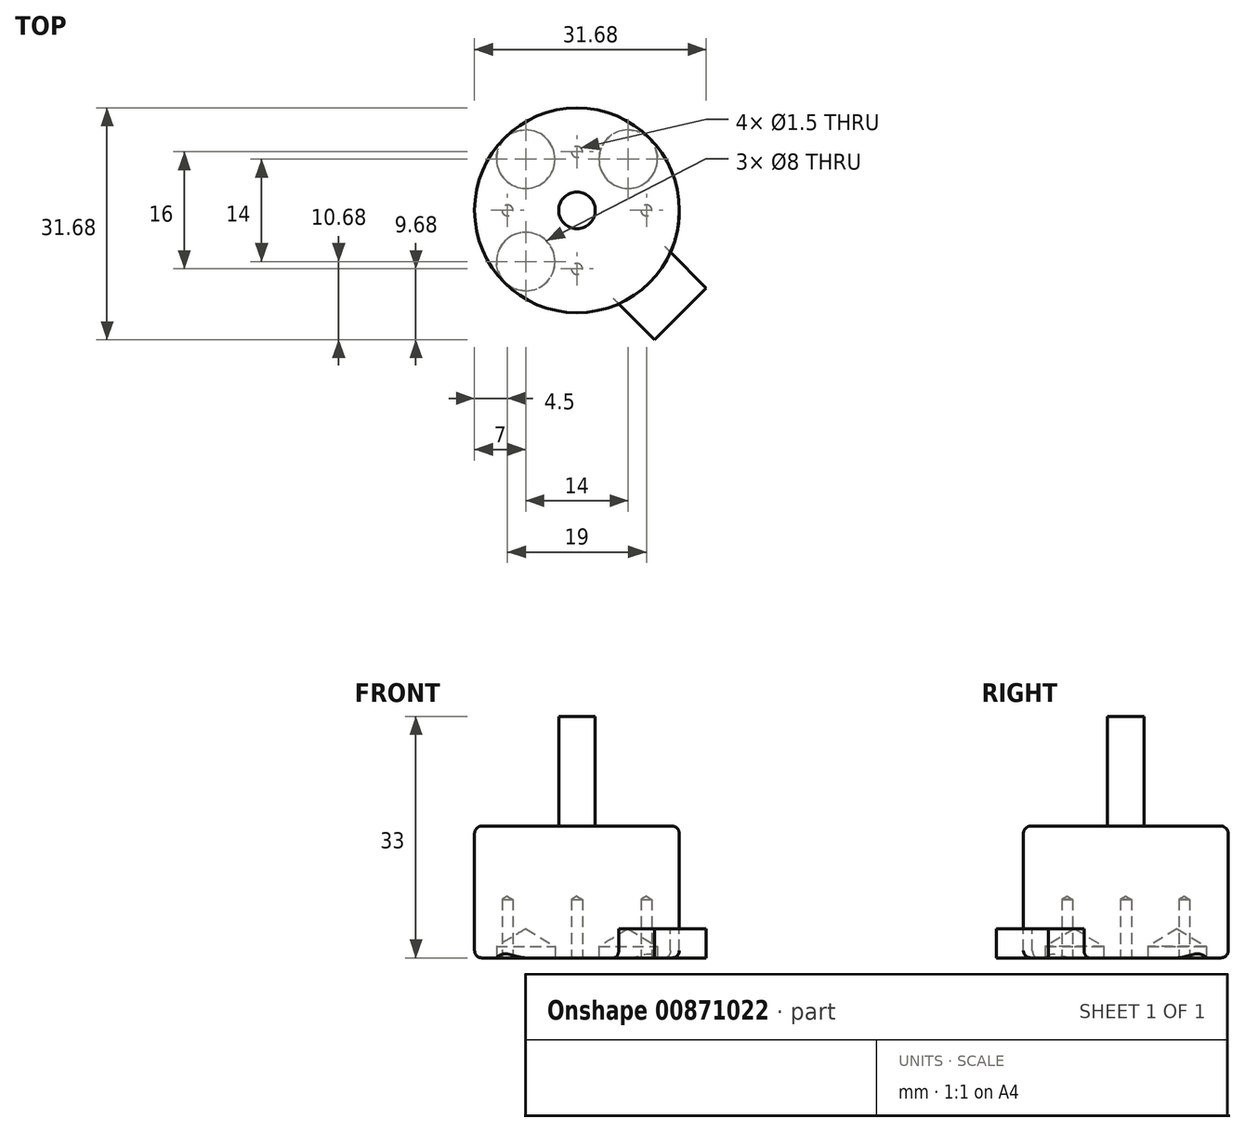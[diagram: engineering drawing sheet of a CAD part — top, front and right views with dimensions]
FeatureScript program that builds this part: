
annotation { "Feature Type Name" : "Feature", "Feature Type Description" : "" }
export const myFeature = defineFeature(function(context is Context, id is Id, definition is map)
    precondition{}
    {
        {
            var Q0;
            Q0=qCreatedBy(makeId("Front.planeOp"),FACE);
            var sketch = newSketch(context, id + "F0", { "sketchPlane" : qUnion([Q0])});
            skLineSegment(sketch, "E0", {"start": v(0, 0) * mm, "end": v(13, 0) * mm});
            skLineSegment(sketch, "E1", {"start": v(14, 1) * mm, "end": v(14, 17) * mm});
            skLineSegment(sketch, "E2", {"start": v(13, 18) * mm, "end": v(2.5, 18) * mm});
            skLineSegment(sketch, "E3", {"start": v(2.5, 18) * mm, "end": v(2.5, 33) * mm});
            skLineSegment(sketch, "E4", {"start": v(2.5, 33) * mm, "end": v(0, 33) * mm});
            skLineSegment(sketch, "E5", {"start": v(0, 33) * mm, "end": v(0, 0) * mm});
            skPoint(sketch, "E6.visualSharp", {"position": v(14, 18) * mm});
            skArc(sketch, "E6.filletArc", {"start": v(14, 17) * mm, "mid": v(13.7, 17.7) * mm, "end": v(13, 18) * mm});
            skPoint(sketch, "E7.visualSharp", {"position": v(14, 0) * mm});
            skArc(sketch, "E7.filletArc", {"start": v(13, 0) * mm, "mid": v(13.7, 0.3) * mm, "end": v(14, 1) * mm});
            skSolve(sketch);
        }
        {
            var Q0;
            Q0=makeQuery(id+"F0.imprint","IMPRINT",FACE,{"disambiguationData":[TD([[makeQuery(id+"F0.imprint","IMPRINT",EDGE,{"derivedFrom":sQuery(id+"F0.wireOp",EDGE,"E0")}),1.0]])]});
            var Q1;
            Q1=sQuery(id+"F0.wireOp",EDGE,"E5");
            revolve(context, id + "F1", {"surfaceOperationType" : NewSurfaceOperationType.NEW, "entities" : qUnion([Q0]), "axis" : qUnion([Q1]), "revolveType" : RevolveType.FULL});
        }
        {
            var Q0;
            Q0=makeQuery(id+"F1.opRevolve","SWEPT_FACE",FACE,{"disambiguationData":[OSD([sQuery(id+"F0.wireOp",EDGE,"E0")])]});
            var sketch = newSketch(context, id + "F2", { "sketchPlane" : qUnion([Q0])});
            skPoint(sketch, "E8", {"position": v(0, 8) * mm});
            skPoint(sketch, "E9", {"position": v(0, -8) * mm});
            skPoint(sketch, "E10", {"position": v(-9.5, 0) * mm});
            skPoint(sketch, "E11", {"position": v(9.5, 0) * mm});
            skSolve(sketch);
        }
        {
            var Q0;
            Q0=sQuery(id+"F2.wireOp",VERTEX,"E8");
            var Q1;
            Q1=sQuery(id+"F2.wireOp",VERTEX,"E10");
            var Q2;
            Q2=sQuery(id+"F2.wireOp",VERTEX,"E9");
            var Q3;
            Q3=sQuery(id+"F2.wireOp",VERTEX,"E11");
            var Q4;
            Q4=makeQuery(id+"F1.opRevolve","SWEPT_BODY",BODY,{"disambiguationData":[OSD([sQuery(id+"F0.wireOp",EDGE,"E0"),sQuery(id+"F0.wireOp",EDGE,"E1"),sQuery(id+"F0.wireOp",EDGE,"E2"),sQuery(id+"F0.wireOp",EDGE,"E3"),sQuery(id+"F0.wireOp",EDGE,"E4"),sQuery(id+"F0.wireOp",EDGE,"E5"),sQuery(id+"F0.wireOp",EDGE,"E6.filletArc"),sQuery(id+"F0.wireOp",EDGE,"E7.filletArc")])]});
            hole(context, id + "F3", {"style" : HoleStyle.SIMPLE, "endStyle" : HoleEndStyle.BLIND, "holeDiameter" : 1.5 * mm, "majorDiameter" : 5 * mm, "holeDepth" : 8 * mm, "isTappedThrough" : true, "tappedDepth" : 12 * mm, "tapClearance" : 3, "locations" : qUnion([Q0, Q1, Q2, Q3]), "scope" : qUnion([Q4])});
        }
        {
            var Q0;
            Q0=makeQuery(id+"F1.opRevolve","SWEPT_FACE",FACE,{"disambiguationData":[OSD([sQuery(id+"F0.wireOp",EDGE,"E0")])]});
            var sketch = newSketch(context, id + "F4", { "sketchPlane" : qUnion([Q0])});
            skLineSegment(sketch, "E12", {"start": v(20.5, 0) * mm, "end": v(0, 0) * mm});
            skLineSegment(sketch, "E13", {"start": v(0, 0) * mm, "end": v(16.66, 16.66) * mm});
            skPoint(sketch, "E14", {"position": v(16.66, 16.66) * mm});
            skSolve(sketch);
        }
        {
            var Q0;
            Q0=makeQuery(id+"F1.opRevolve","SWEPT_FACE",FACE,{"disambiguationData":[OSD([sQuery(id+"F0.wireOp",EDGE,"E4")])]});
            var sketch = newSketch(context, id + "F5", { "sketchPlane" : qUnion([Q0])});
            skPoint(sketch, "E15", {"position": v(0, 0) * mm});
            skSolve(sketch);
        }
        {
            var Q0;
            Q0=sQuery(id+"F5.wireOp",VERTEX,"E15");
            var Q1;
            Q1=sQuery(id+"F4.wireOp",VERTEX,"E12.end");
            var Q2;
            Q2=sQuery(id+"F4.wireOp",VERTEX,"E14");
            cPlane(context, id + "F6", {"entities" : qUnion([Q0, Q1, Q2]), "cplaneType" : CPlaneType.THREE_POINT, "offset" : 25 * mm, "width" : 150 * mm, "height" : 150 * mm});
        }
        {
            var Q0;
            Q0=qCreatedBy(id+"F6.planeOp",FACE);
            var sketch = newSketch(context, id + "F7", { "sketchPlane" : qUnion([Q0])});
            skLineSegment(sketch, "E16.bottom", {"start": v(-11, 0) * mm, "end": v(-20, 0) * mm});
            skLineSegment(sketch, "E16.top", {"start": v(-11, 4) * mm, "end": v(-20, 4) * mm});
            skLineSegment(sketch, "E16.left", {"start": v(-11, 0) * mm, "end": v(-11, 4) * mm});
            skLineSegment(sketch, "E16.right", {"start": v(-20, 0) * mm, "end": v(-20, 4) * mm});
            skSolve(sketch);
        }
        {
            var Q0;
            Q0=makeQuery(id+"F7.imprint","IMPRINT",FACE,{"disambiguationData":[TD([[makeQuery(id+"F7.imprint","IMPRINT",EDGE,{"derivedFrom":sQuery(id+"F7.wireOp",EDGE,"E16.bottom")}),-1.0]])]});
            extrude(context, id + "F8", {"entities" : qUnion([Q0]), "operationType" : NewBodyOperationType.ADD, "endBound" : BoundingType.SYMMETRIC, "depth" : 10 * mm, "offsetDistance" : 25 * mm});
        }
        {
            var Q0;
            Q0=makeQuery(id+"F8.boolean.opBoolean","MERGE",FACE,{"derivedFrom":[makeQuery(id+"F1.opRevolve","SWEPT_FACE",FACE,{"disambiguationData":[OSD([sQuery(id+"F0.wireOp",EDGE,"E0")])]}),makeQuery(id+"F8.opExtrude","SWEPT_FACE",FACE,{"disambiguationData":[OSD([sQuery(id+"F7.wireOp",EDGE,"E16.bottom")])]})]});
            var sketch = newSketch(context, id + "F9", { "sketchPlane" : qUnion([Q0])});
            skLineSegment(sketch, "E17", {"start": v(0, 0) * mm, "end": v(-13.01, 13.01) * mm});
            skLineSegment(sketch, "E18", {"start": v(0, 0) * mm, "end": v(-13.82, -13.82) * mm});
            skLineSegment(sketch, "E19", {"start": v(0, 0) * mm, "end": v(14.67, -14.67) * mm});
            skPoint(sketch, "E20", {"position": v(-7, 7) * mm});
            skPoint(sketch, "E21", {"position": v(-7, -7) * mm});
            skPoint(sketch, "E22", {"position": v(7, -7) * mm});
            skSolve(sketch);
        }
        {
            var Q0;
            Q0=sQuery(id+"F9.wireOp",VERTEX,"E20");
            var Q1;
            Q1=sQuery(id+"F9.wireOp",VERTEX,"E21");
            var Q2;
            Q2=sQuery(id+"F9.wireOp",VERTEX,"E22");
            var Q3;
            Q3=makeQuery(id+"F1.opRevolve","SWEPT_BODY",BODY,{"disambiguationData":[OSD([sQuery(id+"F0.wireOp",EDGE,"E0"),sQuery(id+"F0.wireOp",EDGE,"E1"),sQuery(id+"F0.wireOp",EDGE,"E2"),sQuery(id+"F0.wireOp",EDGE,"E3"),sQuery(id+"F0.wireOp",EDGE,"E4"),sQuery(id+"F0.wireOp",EDGE,"E5"),sQuery(id+"F0.wireOp",EDGE,"E6.filletArc"),sQuery(id+"F0.wireOp",EDGE,"E7.filletArc")])]});
            hole(context, id + "F10", {"style" : HoleStyle.SIMPLE, "endStyle" : HoleEndStyle.BLIND, "holeDiameter" : 8 * mm, "majorDiameter" : 5 * mm, "holeDepth" : 1 * mm, "isTappedThrough" : true, "tappedDepth" : 12 * mm, "tapClearance" : 3, "locations" : qUnion([Q0, Q1, Q2]), "scope" : qUnion([Q3])});
        }
    });
